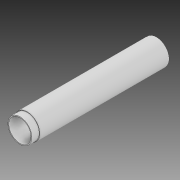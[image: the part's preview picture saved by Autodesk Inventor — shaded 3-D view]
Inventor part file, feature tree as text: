
AUTODESK INVENTOR PART (.ipt)
format: ipt  version: 2020 (Build 240168000, 168)  size: 102,912 bytes
history: native  units: mm
features: revolve x1, sketch x1
ambient origin geometry x8: Origin, YZ Plane, XZ Plane, XY Plane, X Axis, Y Axis, Z Axis, Center Point
bodies: Solid1 (feature_tree)
feature tree (2):
  revolve  "Revolution1"  [1 undecoded]
  sketch  "Sketch1"  dims[d0=6.95mm d1=6.6mm d2=4.0mm d4=76.9mm d5=2.25mm d6=1.5mm d7=2.0mm d8=90.0deg d9=0.5mm d10=15.0mm]
note: 1 required parameter value undecoded (feature->parameter linkage not recoverable at this tier; creation-order binding heuristic only, values carry confidence <= 0.55)
